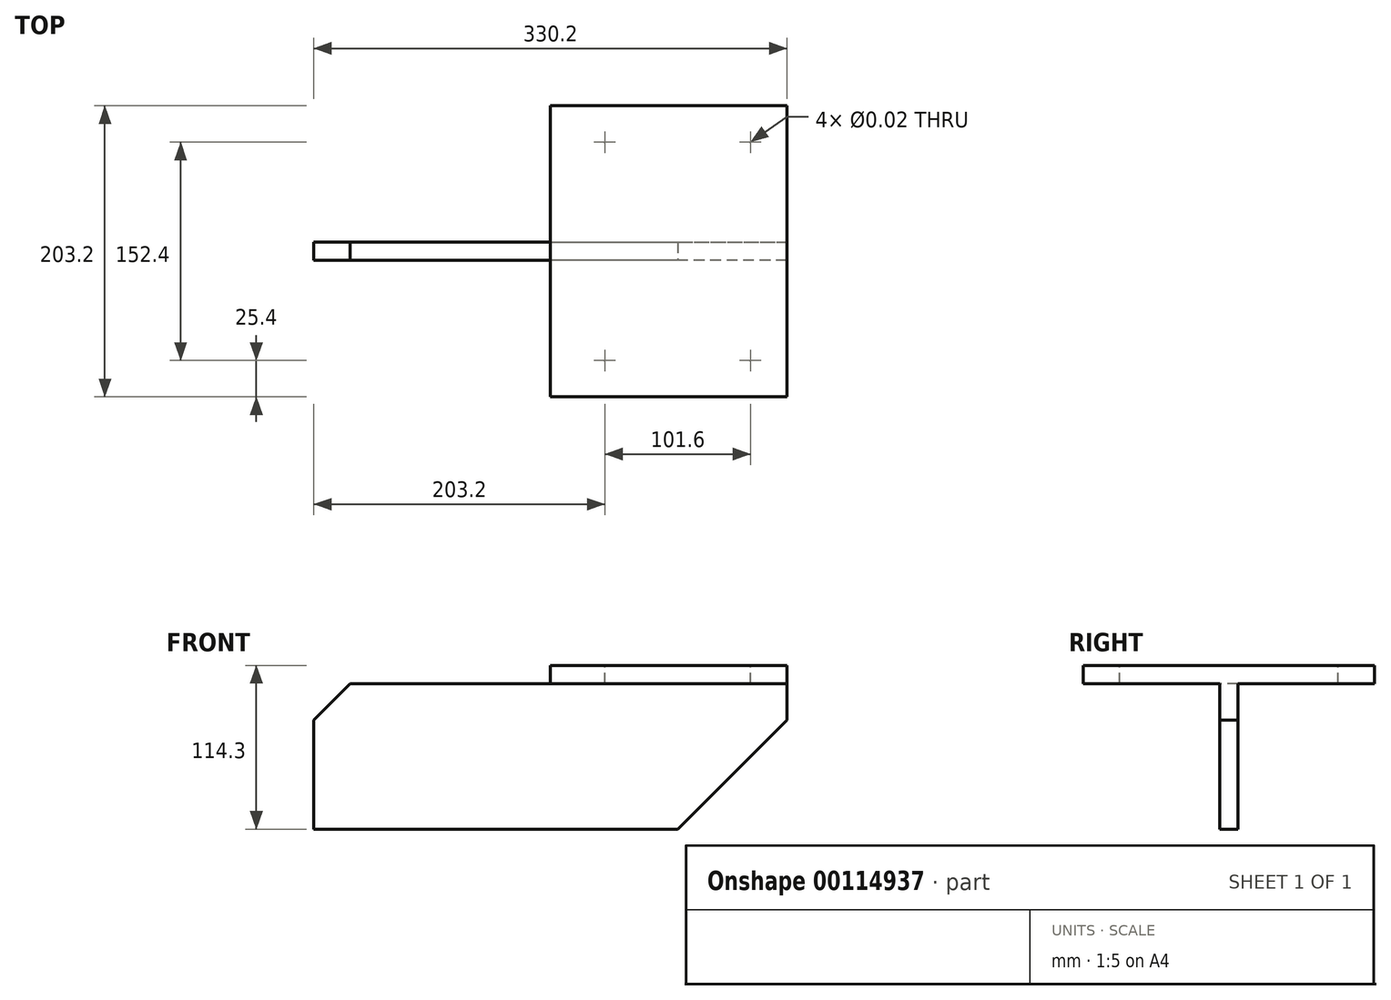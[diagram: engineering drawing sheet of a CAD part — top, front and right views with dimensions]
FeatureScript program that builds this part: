
annotation { "Feature Type Name" : "Feature", "Feature Type Description" : "" }
export const myFeature = defineFeature(function(context is Context, id is Id, definition is map)
    precondition{}
    {
        {
            var Q0;
            Q0=qCreatedBy(makeId("Top.planeOp"),FACE);
            var sketch = newSketch(context, id + "F0", { "sketchPlane" : qUnion([Q0])});
            skLineSegment(sketch, "E0.bottom", {"start": v(-82.55, 101.6) * mm, "end": v(82.55, 101.6) * mm});
            skLineSegment(sketch, "E0.top", {"start": v(-82.55, -101.6) * mm, "end": v(82.55, -101.6) * mm});
            skLineSegment(sketch, "E0.left", {"start": v(-82.55, 101.6) * mm, "end": v(-82.55, -101.6) * mm});
            skLineSegment(sketch, "E0.right", {"start": v(82.55, 101.6) * mm, "end": v(82.55, -101.6) * mm});
            skPoint(sketch, "E0.middle", {"position": v(0, 0) * mm});
            skSolve(sketch);
        }
        {
            var Q0;
            Q0 = qSketchRegion(id + "F0", true);
            extrude(context, id + "F1", {"entities" : qUnion([Q0]), "depth" : 12.7 * mm});
        }
        {
            var Q0;
            Q0=makeQuery(id+"F1.opExtrude","CAP_FACE",FACE,{"disambiguationData":[OSD([sQuery(id+"F0.wireOp",EDGE,"E0.bottom"),sQuery(id+"F0.wireOp",EDGE,"E0.top"),sQuery(id+"F0.wireOp",EDGE,"E0.left"),sQuery(id+"F0.wireOp",EDGE,"E0.right")])],"isStart":false});
            var sketch = newSketch(context, id + "F2", { "sketchPlane" : qUnion([Q0])});
            skLineSegment(sketch, "E1.0", {"start": v(82.55, 101.6) * mm, "end": v(82.55, -101.6) * mm, "construction": true});
            skLineSegment(sketch, "E2.0", {"start": v(57.15, 101.6) * mm, "end": v(57.15, -101.6) * mm, "construction": true});
            skLineSegment(sketch, "E3.0", {"start": v(-44.45, 101.6) * mm, "end": v(-44.45, -101.6) * mm, "construction": true});
            skLineSegment(sketch, "E4", {"start": v(82.55, 0) * mm, "end": v(-97.32, 0) * mm, "construction": true});
            skPoint(sketch, "E4.endSnap0", {"position": v(-82.55, 0) * mm});
            skLineSegment(sketch, "E5.0", {"start": v(82.55, -76.2) * mm, "end": v(-97.32, -76.2) * mm, "construction": true});
            skPoint(sketch, "E6", {"position": v(-44.45, -76.2) * mm});
            skPoint(sketch, "E7", {"position": v(57.15, -76.2) * mm});
            skPoint(sketch, "E8.MirrorP", {"position": v(-44.45, 76.2) * mm});
            skPoint(sketch, "E9.MirrorP", {"position": v(57.15, 76.2) * mm});
            skSolve(sketch);
        }
        {
            var Q0;
            Q0=sQuery(id+"F2.wireOp",VERTEX,"E8.MirrorP");
            var Q1;
            Q1=sQuery(id+"F2.wireOp",VERTEX,"E9.MirrorP");
            var Q2;
            Q2=sQuery(id+"F2.wireOp",VERTEX,"E6");
            var Q3;
            Q3=sQuery(id+"F2.wireOp",VERTEX,"E7");
            var Q4;
            Q4=makeQuery(id+"F1.opExtrude","SWEPT_BODY",BODY,{"disambiguationData":[OSD([sQuery(id+"F0.wireOp",EDGE,"E0.bottom"),sQuery(id+"F0.wireOp",EDGE,"E0.top"),sQuery(id+"F0.wireOp",EDGE,"E0.left"),sQuery(id+"F0.wireOp",EDGE,"E0.right")])]});
            hole(context, id + "F3", {"style" : HoleStyle.SIMPLE, "endStyle" : HoleEndStyle.BLIND, "standardTappedOrClearance" : lookupTablePath({ "standard" : "ANSI", "size" : "9/16 (0.56)", "type" : "Drilled" }), "standardBlindInLast" : lookupTablePath({ "standard" : "ANSI", "size" : "9/16", "type" : "Drilled" }), "holeDiameter" : 9 / 406.4 * mm, "holeDepth" : 50.8 * mm, "locations" : qUnion([Q0, Q1, Q2, Q3]), "scope" : qUnion([Q4])});
        }
        {
            var Q0;
            Q0=makeQuery(id+"F1.opExtrude","CAP_FACE",FACE,{"disambiguationData":[OSD([sQuery(id+"F0.wireOp",EDGE,"E0.bottom"),sQuery(id+"F0.wireOp",EDGE,"E0.top"),sQuery(id+"F0.wireOp",EDGE,"E0.left"),sQuery(id+"F0.wireOp",EDGE,"E0.right")])],"isStart":true});
            var sketch = newSketch(context, id + "F4", { "sketchPlane" : qUnion([Q0])});
            skLineSegment(sketch, "E10.0", {"start": v(-82.55, -101.6) * mm, "end": v(-82.55, 101.6) * mm, "construction": true});
            skLineSegment(sketch, "E11.0", {"start": v(82.55, -101.6) * mm, "end": v(82.55, 101.6) * mm, "construction": true});
            skLineSegment(sketch, "E12.0", {"start": v(-247.65, -101.6) * mm, "end": v(-247.65, 101.6) * mm, "construction": true});
            skLineSegment(sketch, "E13", {"start": v(97.8, 0) * mm, "end": v(-277.88, 0) * mm, "construction": true});
            skLineSegment(sketch, "E14.0", {"start": v(97.8, 6.35) * mm, "end": v(-277.88, 6.35) * mm});
            skLineSegment(sketch, "E15.bottom", {"start": v(-247.65, 6.35) * mm, "end": v(82.55, 6.35) * mm});
            skLineSegment(sketch, "E15.top", {"start": v(-247.65, -6.35) * mm, "end": v(82.55, -6.35) * mm});
            skLineSegment(sketch, "E15.left", {"start": v(-247.65, 6.35) * mm, "end": v(-247.65, -6.35) * mm});
            skLineSegment(sketch, "E15.right", {"start": v(82.55, 6.35) * mm, "end": v(82.55, -6.35) * mm});
            skSolve(sketch);
        }
        {
            var Q0;
            Q0 = qSketchRegion(id + "F4", true);
            extrude(context, id + "F5", {"entities" : qUnion([Q0]), "operationType" : NewBodyOperationType.ADD, "depth" : 101.6 * mm});
        }
        {
            var Q0;
            Q0=makeQuery(id+"F5.opExtrude","CAP_EDGE",EDGE,{"disambiguationData":[OSD([sQuery(id+"F4.wireOp",EDGE,"E15.right")])],"isStart":false});
            chamfer(context, id + "F6", {"entities" : qUnion([Q0]), "width" : 76.2 * mm, "tangentPropagation" : true});
        }
        {
            var Q0;
            Q0=makeQuery(id+"F5.opExtrude","CAP_EDGE",EDGE,{"disambiguationData":[OSD([sQuery(id+"F4.wireOp",EDGE,"E15.left")])],"isStart":true});
            chamfer(context, id + "F7", {"entities" : qUnion([Q0]), "width" : 25.4 * mm, "tangentPropagation" : true});
        }
    });
